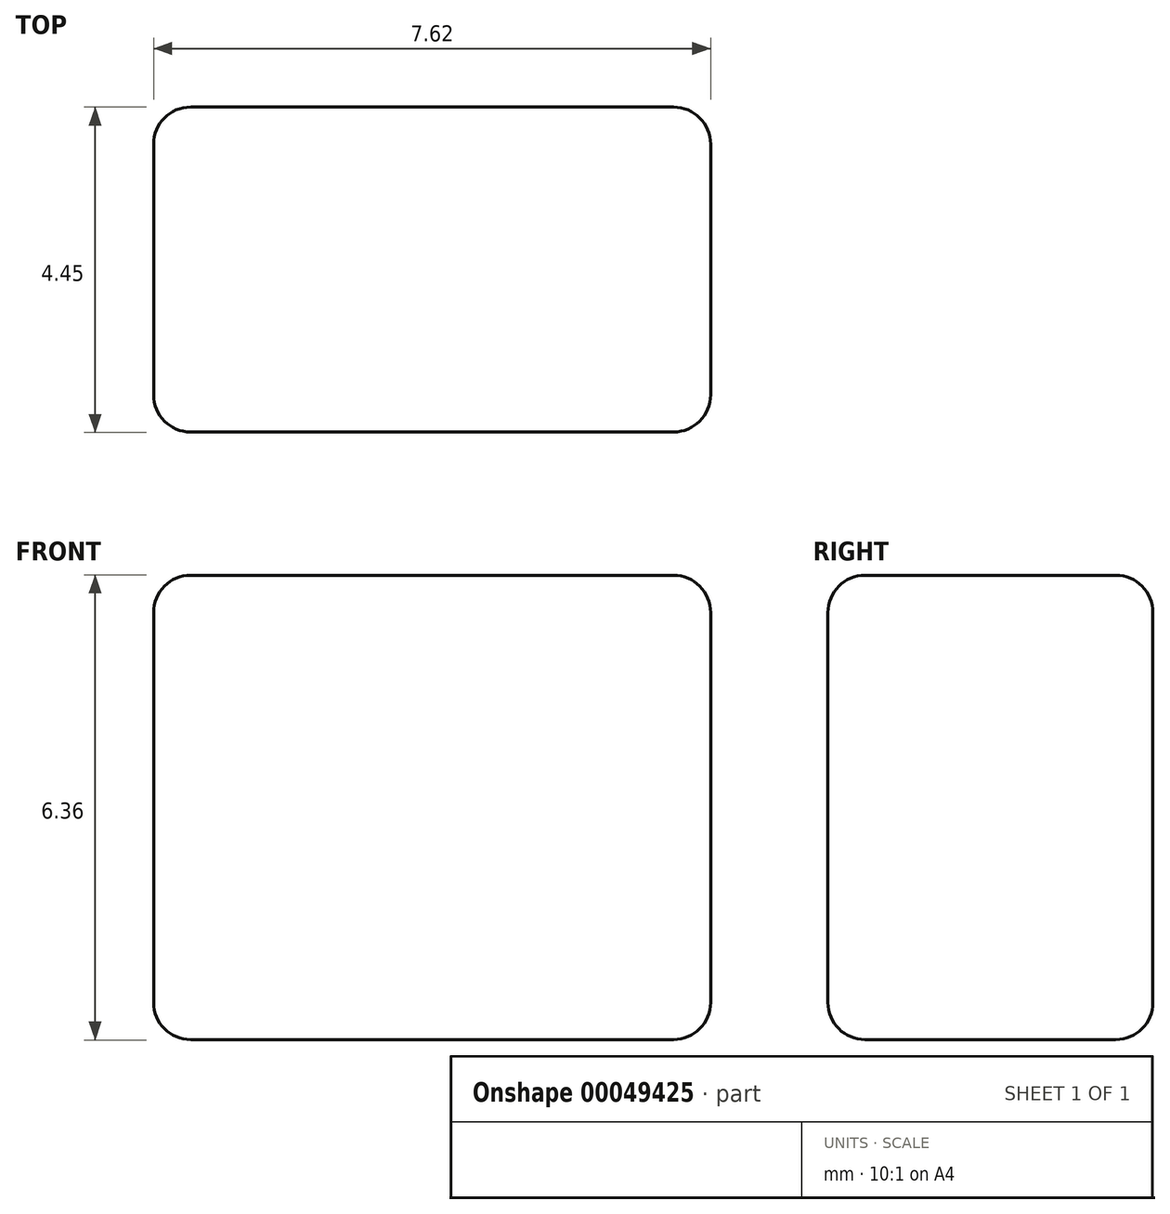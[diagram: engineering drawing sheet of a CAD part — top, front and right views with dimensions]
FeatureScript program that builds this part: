
annotation { "Feature Type Name" : "Feature", "Feature Type Description" : "" }
export const myFeature = defineFeature(function(context is Context, id is Id, definition is map)
    precondition{}
    {
        {
            var Q0;
            Q0=qCreatedBy(makeId("Front.planeOp"),FACE);
            var sketch = newSketch(context, id + "F0", { "sketchPlane" : qUnion([Q0])});
            skLineSegment(sketch, "E0.rect.bottom", {"start": v(3.81, 3.18) * mm, "end": v(-3.81, 3.18) * mm});
            skLineSegment(sketch, "E0.rect.top", {"start": v(3.81, -3.18) * mm, "end": v(-3.81, -3.18) * mm});
            skLineSegment(sketch, "E0.rect.left", {"start": v(3.81, 3.18) * mm, "end": v(3.81, -3.17) * mm});
            skLineSegment(sketch, "E0.rect.right", {"start": v(-3.8, 3.17) * mm, "end": v(-3.81, -3.18) * mm});
            skPoint(sketch, "E0.rect.middle", {"position": v(0, 0) * mm});
            skSolve(sketch);
        }
        {
            var Q0;
            Q0 = qSketchRegion(id + "F0", true);
            extrude(context, id + "F1", {"entities" : qUnion([Q0]), "depth" : 4.44 * mm});
        }
        {
            var Q0;
            Q0=makeQuery(id+"F1.opExtrude","SWEPT_EDGE",EDGE,{"disambiguationData":[OSD([sQuery(id+"F0.wireOp",EDGE,"E0.rect.bottom"),sQuery(id+"F0.wireOp",EDGE,"E0.rect.right")])]});
            var Q1;
            Q1=makeQuery(id+"F1.opExtrude","SWEPT_EDGE",EDGE,{"disambiguationData":[OSD([sQuery(id+"F0.wireOp",EDGE,"E0.rect.top"),sQuery(id+"F0.wireOp",EDGE,"E0.rect.left")])]});
            var Q2;
            Q2=makeQuery(id+"F1.opExtrude","SWEPT_EDGE",EDGE,{"disambiguationData":[OSD([sQuery(id+"F0.wireOp",EDGE,"E0.rect.top"),sQuery(id+"F0.wireOp",EDGE,"E0.rect.right")])]});
            var Q3;
            Q3=makeQuery(id+"F1.opExtrude","CAP_EDGE",EDGE,{"disambiguationData":[OSD([sQuery(id+"F0.wireOp",EDGE,"E0.rect.bottom")])],"isStart":false});
            var Q4;
            Q4=makeQuery(id+"F1.opExtrude","CAP_EDGE",EDGE,{"disambiguationData":[OSD([sQuery(id+"F0.wireOp",EDGE,"E0.rect.top")])],"isStart":true});
            var Q5;
            Q5=makeQuery(id+"F1.opExtrude","CAP_EDGE",EDGE,{"disambiguationData":[OSD([sQuery(id+"F0.wireOp",EDGE,"E0.rect.top")])],"isStart":false});
            var Q6;
            Q6=makeQuery(id+"F1.opExtrude","CAP_EDGE",EDGE,{"disambiguationData":[OSD([sQuery(id+"F0.wireOp",EDGE,"E0.rect.left")])],"isStart":false});
            var Q7;
            Q7=makeQuery(id+"F1.opExtrude","CAP_EDGE",EDGE,{"disambiguationData":[OSD([sQuery(id+"F0.wireOp",EDGE,"E0.rect.right")])],"isStart":true});
            var Q8;
            Q8=makeQuery(id+"F1.opExtrude","CAP_EDGE",EDGE,{"disambiguationData":[OSD([sQuery(id+"F0.wireOp",EDGE,"E0.rect.right")])],"isStart":false});
            var Q9;
            Q9=makeQuery(id+"F1.opExtrude","SWEPT_EDGE",EDGE,{"disambiguationData":[OSD([sQuery(id+"F0.wireOp",EDGE,"E0.rect.bottom"),sQuery(id+"F0.wireOp",EDGE,"E0.rect.left")])]});
            var Q10;
            Q10=makeQuery(id+"F1.opExtrude","CAP_EDGE",EDGE,{"disambiguationData":[OSD([sQuery(id+"F0.wireOp",EDGE,"E0.rect.bottom")])],"isStart":true});
            var Q11;
            Q11=makeQuery(id+"F1.opExtrude","CAP_EDGE",EDGE,{"disambiguationData":[OSD([sQuery(id+"F0.wireOp",EDGE,"E0.rect.left")])],"isStart":true});
            fillet(context, id + "F2", {"entities" : qUnion([Q0, Q1, Q2, Q3, Q4, Q5, Q6, Q7, Q8, Q9, Q10, Q11]), "radius" : 0.5 * mm, "tangentPropagation" : true, "allowEdgeOverflow" : false});
        }
    });
